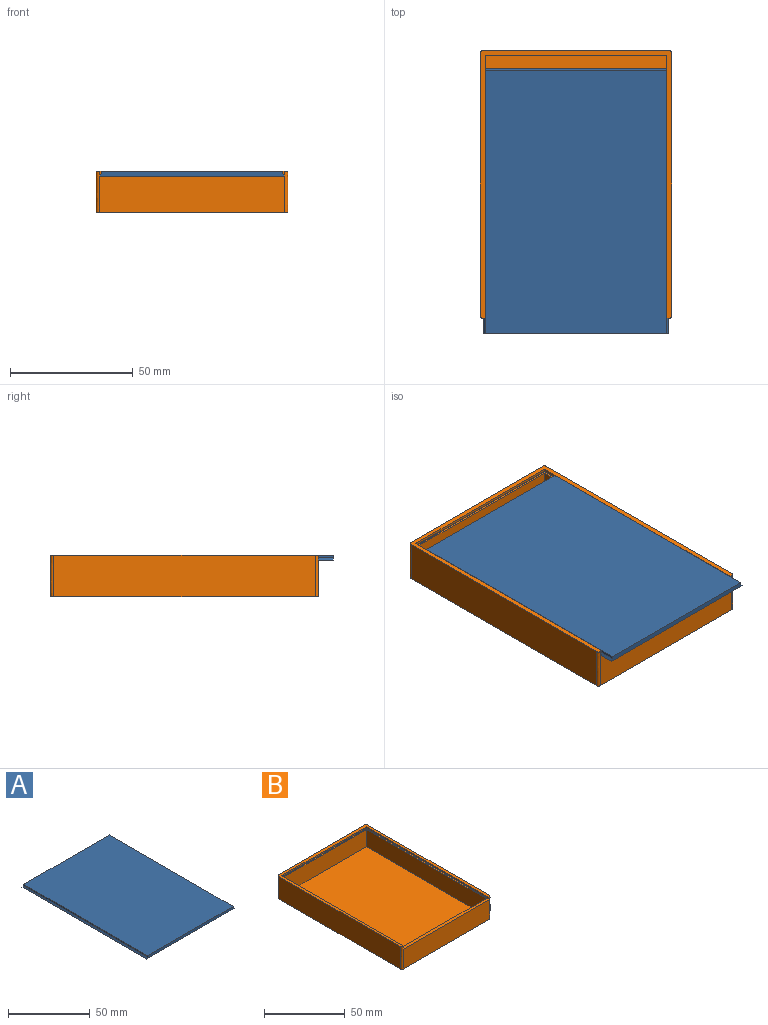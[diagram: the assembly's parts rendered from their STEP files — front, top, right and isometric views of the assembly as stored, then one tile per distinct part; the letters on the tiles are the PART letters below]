
ASSEMBLY  parts=2 mates=1
PART A: 9 faces, bbox 75.4x107.7x2 mm
  f0: plane 106.9x73.8mm, normal (0,0,1), area 7889.2mm2, adj f4,f5,f6,f8
  f1: plane 107.7x1mm, normal (-0.78,0,0.62), area 137.4mm2, adj f2,f5,f6,f7
  f2: plane 107.7x75.4mm, normal (0,0,-1), area 8120.6mm2, adj f1,f3,f6,f7
  f3: plane 107.7x1mm, normal (0.78,0,0.62), area 137.4mm2, adj f2,f4,f6,f7
  f4: plane 106.9x1mm, normal (1,0,0), area 106.9mm2, adj f0,f3,f6,f8
  f5: plane 106.9x1mm, normal (-1,0,0), area 106.9mm2, adj f0,f1,f6,f8
  f6: plane 75.4x2mm, normal (0,-1,0), area 148.4mm2, adj f0,f1,f2,f3,f4,f5
  f7: plane 75.4x1mm, normal (0,0.78,0.62), area 95.5mm2, adj f1,f2,f3,f8
  f8: plane 73.8x1mm, normal (0,1,0), area 73.8mm2, adj f0,f4,f5,f7
PART B: 243 faces, bbox 78x109x18.7 mm
  f0: plane 109x78mm, normal (0,0,-1), area 8437.6mm2, adj f1,f4,f5,f6,f20,f21,f22,f23
  f1: plane 75.6x15mm, normal (0,-1,0), area 1134mm2, adj f0,f3,f22,f23
  f2: plane 2x0.8mm, normal (0,-1,0), area 1.2mm2, adj f13,f14,f15,f23
  f3: plane 107.8x75.6mm, normal (0,0,1), area 379.7mm2, adj f1,f8,f10,f11,f12,f13,f17,f19
  f4: plane 106.6x17mm, normal (-1,0,0), area 1812.2mm2, adj f0,f15,f21,f23
  f5: plane 106.6x17mm, normal (1,0,0), area 1812.2mm2, adj f0,f15,f20,f22
  f6: plane 75.6x17mm, normal (0,1,0), area 1285.2mm2, adj f0,f15,f20,f21
  f7: plane 2x0.8mm, normal (0,-1,0), area 1.2mm2, adj f15,f16,f17,f22
  f8: plane 105x13mm, normal (1,0,0), area 1365mm2, adj f3,f9,f11,f12
  f9: plane 105x74mm, normal (0,0,1), area 7770mm2, adj f8,f10,f11,f12
  f10: plane 105x13mm, normal (-1,0,0), area 1365mm2, adj f3,f9,f11,f12
  f11: plane 74x13mm, normal (0,-1,0), area 962mm2, adj f3,f8,f9,f10
  f12: plane 74x13mm, normal (0,1,0), area 962mm2, adj f3,f8,f9,f10
  f13: plane 107.8x1mm, normal (0.78,0,-0.62), area 137.5mm2, adj f2,f3,f14,f19
  f14: plane 107x1mm, normal (1,0,0), area 107mm2, adj f2,f13,f15,f18
  f15: plane 109x78mm, normal (0,0,1), area 583mm2, adj f2,f4,f5,f6,f7,f14,f16,f18
  f16: plane 107x1mm, normal (-1,0,0), area 107mm2, adj f7,f15,f17,f18
  f17: plane 107.8x1mm, normal (-0.78,0,-0.62), area 137.5mm2, adj f3,f7,f16,f19
  f18: plane 74x1mm, normal (0,-1,0), area 74mm2, adj f14,f15,f16,f19
  f19: plane 75.6x1mm, normal (0,-0.78,-0.62), area 95.8mm2, adj f3,f13,f17,f18
  f20: bspline ~18.7x1.2mm, area 33.1mm2, adj f0,f5,f6,f15
  f21: bspline ~18.7x1.2mm, area 33.1mm2, adj f0,f4,f6,f15
  f22: bspline ~18.7x1.2mm, area 33.1mm2, adj f0,f1,f5,f7,f15
  f23: bspline ~18.7x1.2mm, area 33.1mm2, adj f0,f1,f2,f4,f15
  f24: plane 4.92x1.71mm, normal (0.33,0.94,0), area 5.2mm2, adj f0,f25,f30,f31
  f25: plane 1x0.8mm, normal (1,0,0), area 0.8mm2, adj f0,f24,f26,f31
  f26: plane 4.92x1.72mm, normal (0.33,-0.94,0), area 5.2mm2, adj f0,f25,f27,f31
  f27: plane 1x0.84mm, normal (-1,0,0), area 0.8mm2, adj f0,f26,f28,f31
  f28: plane 3.69x1.29mm, normal (-0.33,0.94,0), area 3.9mm2, adj f0,f27,f29,f31
  f29: plane 3.69x1.28mm, normal (-0.33,-0.95,0), area 3.9mm2, adj f0,f28,f30,f31
  f30: plane 1x0.83mm, normal (-1,0,0), area 0.8mm2, adj f0,f24,f29,f31
  f31: plane 4.92x4.23mm, normal (0,0,-1), area 7.6mm2, adj f24,f25,f26,f27,f28,f29,f30
  f32: plane 1x0.9mm, normal (1,0,0), area 0.9mm2, adj f0,f33,f35,f36
  f33: plane 1x0.54mm, normal (0.33,-0.95,0), area 0.6mm2, adj f0,f32,f34,f36
  f34: plane 1.28x1mm, normal (-1,0,0), area 1.3mm2, adj f0,f33,f35,f36
  f35: plane 1x0.54mm, normal (0.34,0.94,0), area 0.6mm2, adj f0,f32,f34,f36
  f36: plane 1.28x0.54mm, normal (0,0,-1), area 0.6mm2, adj f32,f33,f34,f35
  f37: plane 1.94x1.12mm, normal (0.5,0.87,0), area 2.2mm2, adj f0,f38,f62,f63
  f38: extruded ~1x0.67mm, area 0.9mm2, adj f0,f37,f39,f63
  f39: extruded ~1x0.91mm, area 1mm2, adj f0,f38,f40,f63
  f40: extruded ~1x0.64mm, area 0.7mm2, adj f0,f39,f41,f63
  f41: extruded ~1x0.48mm, area 0.6mm2, adj f0,f40,f42,f63
  f42: extruded ~1x0.55mm, area 0.6mm2, adj f0,f41,f43,f63
  f43: extruded ~1x0.62mm, area 0.6mm2, adj f0,f42,f44,f63
  f44: plane 1x0.34mm, normal (1,0,0), area 0.3mm2, adj f0,f43,f45,f63
  f45: plane 1x0.61mm, normal (0,-1,0), area 0.6mm2, adj f0,f44,f46,f63
  f46: plane 1x0.33mm, normal (-1,0,0), area 0.3mm2, adj f0,f45,f47,f63
  f47: extruded ~1x0.5mm, area 0.5mm2, adj f0,f46,f48,f63
  f48: extruded ~1x0.29mm, area 0.4mm2, adj f0,f47,f49,f63
  f49: extruded ~1x0.3mm, area 0.3mm2, adj f0,f48,f50,f63
  f50: extruded ~1x0.28mm, area 0.3mm2, adj f0,f49,f51,f63
  f51: extruded ~1x0.5mm, area 0.5mm2, adj f0,f50,f52,f63
  f52: extruded ~1x0.32mm, area 0.4mm2, adj f0,f51,f53,f63
  f53: extruded ~1x0.27mm, area 0.3mm2, adj f0,f52,f54,f63
  f54: extruded ~1x0.29mm, area 0.3mm2, adj f0,f53,f55,f63
  f55: plane 1x0.45mm, normal (1,0,0), area 0.5mm2, adj f0,f54,f56,f63
  f56: plane 1x0.59mm, normal (0,-1,0), area 0.6mm2, adj f0,f55,f57,f63
  f57: plane 1x0.24mm, normal (-1,0,0), area 0.2mm2, adj f0,f56,f58,f63
  f58: plane 1x0.14mm, normal (-1,0,0), area 0.1mm2, adj f0,f57,f59,f63
  f59: extruded ~1x0.07mm, area 0.1mm2, adj f0,f58,f60,f63
  f60: extruded ~1x0.04mm, area 0mm2, adj f0,f59,f61,f63
  f61: plane 1.78x1mm, normal (-0.46,-0.89,0), area 2mm2, adj f0,f60,f62,f63
  f62: plane 1x0.85mm, normal (-1,0,0), area 0.8mm2, adj f0,f37,f61,f63
  f63: plane 4.92x2.27mm, normal (0,0,-1), area 4.7mm2, adj f37,f38,f39,f40,f41,f42,f43,f44
  f64: plane 4.92x1mm, normal (0,-1,0), area 4.9mm2, adj f0,f65,f67,f68
  f65: plane 1x0.8mm, normal (-1,0,0), area 0.8mm2, adj f0,f64,f66,f68
  f66: plane 4.92x1mm, normal (0,1,0), area 4.9mm2, adj f0,f65,f67,f68
  f67: plane 1x0.8mm, normal (1,0,0), area 0.8mm2, adj f0,f64,f66,f68
  f68: plane 4.92x0.8mm, normal (0,0,-1), area 3.9mm2, adj f64,f65,f66,f67
  f69: plane 1x0.56mm, normal (-0.75,0.66,0), area 0.7mm2, adj f0,f70,f73,f74
  f70: extruded ~1.26x1mm, area 1.4mm2, adj f0,f69,f71,f74
  f71: plane 1x0.66mm, normal (0,-1,0), area 0.7mm2, adj f0,f70,f72,f74
  f72: extruded ~1x0.37mm, area 0.4mm2, adj f0,f71,f73,f74
  f73: extruded ~1x0.33mm, area 0.4mm2, adj f0,f69,f72,f74
  f74: plane 1.26x1.02mm, normal (0,0,-1), area 0.8mm2, adj f69,f70,f71,f72,f73
  f75: plane 1x0.78mm, normal (0,-1,0), area 0.8mm2, adj f0,f76,f87,f88
  f76: extruded ~1x0.39mm, area 0.5mm2, adj f0,f75,f77,f88
  f77: extruded ~1x0.39mm, area 0.4mm2, adj f0,f76,f78,f88
  f78: extruded ~1x0.73mm, area 1mm2, adj f0,f77,f79,f88
  f79: plane 1x0.64mm, normal (0,-1,0), area 0.6mm2, adj f0,f78,f80,f88
  f80: extruded ~1x0.55mm, area 0.6mm2, adj f0,f79,f81,f88
  f81: extruded ~1x0.4mm, area 0.5mm2, adj f0,f80,f82,f88
  f82: extruded ~1x0.41mm, area 0.5mm2, adj f0,f81,f83,f88
  f83: extruded ~1x0.47mm, area 0.5mm2, adj f0,f82,f84,f88
  f84: extruded ~1x0.58mm, area 0.6mm2, adj f0,f83,f85,f88
  f85: extruded ~1x0.4mm, area 0.5mm2, adj f0,f84,f86,f88
  f86: extruded ~1x0.42mm, area 0.5mm2, adj f0,f85,f87,f88
  f87: extruded ~1x0.45mm, area 0.5mm2, adj f0,f75,f86,f88
  f88: plane 2.83x1.3mm, normal (0,0,-1), area 2.2mm2, adj f75,f76,f77,f78,f79,f80,f81,f82
  f89: plane 1x0.58mm, normal (0.24,-0.97,0), area 0.6mm2, adj f0,f90,f100,f101
  f90: extruded ~1x0.27mm, area 0.3mm2, adj f0,f89,f91,f101
  f91: extruded ~1x0.33mm, area 0.3mm2, adj f0,f90,f92,f101
  f92: extruded ~1x0.34mm, area 0.3mm2, adj f0,f91,f93,f101
  f93: extruded ~1x0.33mm, area 0.3mm2, adj f0,f92,f94,f101
  f94: plane 1x0.01mm, normal (-1,0,0), area 0mm2, adj f0,f93,f95,f101
  f95: plane 1x0.64mm, normal (0,1,0), area 0.6mm2, adj f0,f94,f96,f101
  f96: plane 1x0.02mm, normal (1,0,0), area 0mm2, adj f0,f95,f97,f101
  f97: extruded ~1x0.29mm, area 0.3mm2, adj f0,f96,f98,f101
  f98: extruded ~1x0.31mm, area 0.3mm2, adj f0,f97,f99,f101
  f99: extruded ~1x0.3mm, area 0.3mm2, adj f0,f98,f100,f101
  f100: extruded ~1x0.24mm, area 0.3mm2, adj f0,f89,f99,f101
  f101: plane 1.29x0.93mm, normal (0,0,-1), area 0.8mm2, adj f89,f90,f91,f92,f93,f94,f95,f96
  f102: extruded ~1x0.53mm, area 0.5mm2, adj f0,f103,f115,f116
  f103: extruded ~1x0.39mm, area 0.5mm2, adj f0,f102,f104,f116
  f104: extruded ~1x0.4mm, area 0.5mm2, adj f0,f103,f105,f116
  f105: extruded ~1x0.44mm, area 0.5mm2, adj f0,f104,f106,f116
  f106: plane 1x0.76mm, normal (0,1,0), area 0.8mm2, adj f0,f105,f107,f116
  f107: extruded ~1x0.35mm, area 0.5mm2, adj f0,f106,f108,f116
  f108: extruded ~1x0.42mm, area 0.5mm2, adj f0,f107,f109,f116
  f109: extruded ~1x0.37mm, area 0.4mm2, adj f0,f108,f110,f116
  f110: extruded ~1x0.35mm, area 0.4mm2, adj f0,f109,f111,f116
  f111: plane 1x0.7mm, normal (0,1,0), area 0.7mm2, adj f0,f110,f112,f116
  f112: extruded ~1x0.49mm, area 0.5mm2, adj f0,f111,f113,f116
  f113: extruded ~1x0.4mm, area 0.5mm2, adj f0,f112,f114,f116
  f114: extruded ~1x0.41mm, area 0.5mm2, adj f0,f113,f115,f116
  f115: extruded ~1x0.53mm, area 0.5mm2, adj f0,f102,f114,f116
  f116: plane 2.79x1.26mm, normal (0,0,-1), area 2.1mm2, adj f102,f103,f104,f105,f106,f107,f108,f109
  f117: extruded ~1x0.07mm, area 0.1mm2, adj f0,f118,f127,f128
  f118: extruded ~1x0.15mm, area 0.2mm2, adj f0,f117,f119,f128
  f119: extruded ~1x0.19mm, area 0.2mm2, adj f0,f118,f120,f128
  f120: extruded ~1x0.19mm, area 0.2mm2, adj f0,f119,f121,f128
  f121: extruded ~1x0.49mm, area 0.5mm2, adj f0,f120,f122,f128
  f122: extruded ~1x0.6mm, area 0.6mm2, adj f0,f121,f123,f128
  f123: plane 1x0.67mm, normal (0,-1,0), area 0.7mm2, adj f0,f122,f124,f128
  f124: extruded ~1x0.34mm, area 0.3mm2, adj f0,f123,f125,f128
  f125: extruded ~1x0.22mm, area 0.2mm2, adj f0,f124,f126,f128
  f126: extruded ~1x0.13mm, area 0.1mm2, adj f0,f125,f127,f128
  f127: extruded ~1x0.08mm, area 0.1mm2, adj f0,f117,f126,f128
  f128: plane 1.09x0.84mm, normal (0,0,-1), area 0.6mm2, adj f117,f118,f119,f120,f121,f122,f123,f124
  f129: plane 1.99x1mm, normal (1,0,0), area 2mm2, adj f0,f130,f132,f133
  f130: plane 1x0.61mm, normal (0,-1,0), area 0.6mm2, adj f0,f129,f131,f133
  f131: plane 1.99x1mm, normal (-1,0,0), area 2mm2, adj f0,f130,f132,f133
  f132: plane 1x0.61mm, normal (0,1,0), area 0.6mm2, adj f0,f129,f131,f133
  f133: plane 1.99x0.61mm, normal (0,0,-1), area 1.2mm2, adj f129,f130,f131,f132
  f134: plane 1x0.61mm, normal (0,-1,0), area 0.6mm2, adj f0,f135,f137,f138
  f135: plane 1.99x1mm, normal (-1,0,0), area 2mm2, adj f0,f134,f136,f138
  f136: plane 1x0.61mm, normal (0,1,0), area 0.6mm2, adj f0,f135,f137,f138
  f137: plane 1.99x1mm, normal (1,0,0), area 2mm2, adj f0,f134,f136,f138
  f138: plane 1.99x0.61mm, normal (0,0,-1), area 1.2mm2, adj f134,f135,f136,f137
  f139: plane 1x0.55mm, normal (0,1,0), area 0.5mm2, adj f0,f140,f142,f143
  f140: plane 1.78x1mm, normal (1,0,0), area 1.8mm2, adj f0,f139,f141,f143
  f141: plane 1x0.55mm, normal (0,-1,0), area 0.5mm2, adj f0,f140,f142,f143
  f142: plane 1.78x1mm, normal (-1,0,0), area 1.8mm2, adj f0,f139,f141,f143
  f143: plane 1.78x0.55mm, normal (0,0,-1), area 1mm2, adj f139,f140,f141,f142
  f144: plane 1x0.66mm, normal (0,-1,0), area 0.7mm2, adj f0,f145,f149,f150
  f145: extruded ~1x0.69mm, area 0.7mm2, adj f0,f144,f146,f150
  f146: extruded ~1x0.57mm, area 0.7mm2, adj f0,f145,f147,f150
  f147: plane 1x0.56mm, normal (0.75,0.66,0), area 0.7mm2, adj f0,f146,f148,f150
  f148: extruded ~1x0.32mm, area 0.4mm2, adj f0,f147,f149,f150
  f149: extruded ~1x0.38mm, area 0.4mm2, adj f0,f144,f148,f150
  f150: plane 1.26x1.02mm, normal (0,0,-1), area 0.8mm2, adj f144,f145,f146,f147,f148,f149
  f151: extruded ~1.05x1mm, area 1.1mm2, adj f0,f152,f168,f169
  f152: extruded ~1x0.77mm, area 0.9mm2, adj f0,f151,f153,f169
  f153: extruded ~1x0.6mm, area 0.8mm2, adj f0,f152,f154,f169
  f154: extruded ~1x0.75mm, area 0.8mm2, adj f0,f153,f155,f169
  f155: plane 1x0.66mm, normal (0,1,0), area 0.7mm2, adj f0,f154,f156,f169
  f156: extruded ~1x0.41mm, area 0.4mm2, adj f0,f155,f157,f169
  f157: extruded ~1x0.35mm, area 0.5mm2, adj f0,f156,f158,f169
  f158: extruded ~1x0.56mm, area 0.6mm2, adj f0,f157,f159,f169
  f159: extruded ~1x0.8mm, area 0.8mm2, adj f0,f158,f160,f169
  f160: extruded ~1x0.8mm, area 0.8mm2, adj f0,f159,f161,f169
  f161: extruded ~1x0.56mm, area 0.6mm2, adj f0,f160,f162,f169
  f162: extruded ~1x0.34mm, area 0.5mm2, adj f0,f161,f163,f169
  f163: extruded ~1x0.41mm, area 0.4mm2, adj f0,f162,f164,f169
  f164: plane 1x0.67mm, normal (0,1,0), area 0.7mm2, adj f0,f163,f165,f169
  f165: extruded ~1x0.75mm, area 0.8mm2, adj f0,f164,f166,f169
  f166: extruded ~1x0.6mm, area 0.8mm2, adj f0,f165,f167,f169
  f167: extruded ~1x0.77mm, area 0.9mm2, adj f0,f166,f168,f169
  f168: extruded ~1.05x1mm, area 1.1mm2, adj f0,f151,f167,f169
  f169: plane 5.02x1.89mm, normal (0,0,-1), area 4.4mm2, adj f151,f152,f153,f154,f155,f156,f157,f158
  f170: plane 2.36x1mm, normal (0,1,0), area 2.4mm2, adj f0,f171,f181,f182
  f171: plane 1x0.81mm, normal (1,0,0), area 0.8mm2, adj f0,f170,f172,f182
  f172: plane 2.44x1mm, normal (0,-1,0), area 2.4mm2, adj f0,f171,f173,f182
  f173: extruded ~1.06x1mm, area 1.1mm2, adj f0,f172,f174,f182
  f174: extruded ~1x0.78mm, area 0.9mm2, adj f0,f173,f175,f182
  f175: extruded ~1x0.56mm, area 0.7mm2, adj f0,f174,f176,f182
  f176: extruded ~1x0.74mm, area 0.8mm2, adj f0,f175,f177,f182
  f177: plane 1x0.66mm, normal (0,1,0), area 0.7mm2, adj f0,f176,f178,f182
  f178: extruded ~1x0.4mm, area 0.4mm2, adj f0,f177,f179,f182
  f179: extruded ~1x0.34mm, area 0.5mm2, adj f0,f178,f180,f182
  f180: extruded ~1x0.59mm, area 0.6mm2, adj f0,f179,f181,f182
  f181: extruded ~1x0.87mm, area 0.9mm2, adj f0,f170,f180,f182
  f182: plane 4.96x1.78mm, normal (0,0,-1), area 4.1mm2, adj f170,f171,f172,f173,f174,f175,f176,f177
  f183: plane 1x0.81mm, normal (1,0,0), area 0.8mm2, adj f0,f184,f194,f195
  f184: plane 2.36x1mm, normal (0,-1,0), area 2.4mm2, adj f0,f183,f185,f195
  f185: extruded ~1x0.88mm, area 0.9mm2, adj f0,f184,f186,f195
  f186: extruded ~1x0.58mm, area 0.6mm2, adj f0,f185,f187,f195
  f187: extruded ~1x0.34mm, area 0.5mm2, adj f0,f186,f188,f195
  f188: extruded ~1x0.4mm, area 0.4mm2, adj f0,f187,f189,f195
  f189: plane 1x0.66mm, normal (0,-1,0), area 0.7mm2, adj f0,f188,f190,f195
  f190: extruded ~1x0.74mm, area 0.8mm2, adj f0,f189,f191,f195
  f191: extruded ~1x0.56mm, area 0.7mm2, adj f0,f190,f192,f195
  f192: extruded ~1x0.78mm, area 0.9mm2, adj f0,f191,f193,f195
  f193: extruded ~1.06x1mm, area 1.1mm2, adj f0,f192,f194,f195
  f194: plane 2.44x1mm, normal (0,1,0), area 2.4mm2, adj f0,f183,f193,f195
  f195: plane 4.96x1.78mm, normal (0,0,-1), area 4.1mm2, adj f183,f184,f185,f186,f187,f188,f189,f190
  f196: plane 1x0.82mm, normal (1,0,0), area 0.8mm2, adj f0,f197,f201,f202
  f197: plane 4.92x1mm, normal (0,-1,0), area 4.9mm2, adj f0,f196,f198,f202
  f198: plane 3.08x1mm, normal (-1,0,0), area 3.1mm2, adj f0,f197,f199,f202
  f199: plane 1x0.61mm, normal (0,1,0), area 0.6mm2, adj f0,f198,f200,f202
  f200: plane 2.27x1mm, normal (1,0,0), area 2.3mm2, adj f0,f199,f201,f202
  f201: plane 4.32x1mm, normal (0,1,0), area 4.3mm2, adj f0,f196,f200,f202
  f202: plane 4.92x3.08mm, normal (0,0,-1), area 5.4mm2, adj f196,f197,f198,f199,f200,f201
  f203: plane 3.75x1mm, normal (1,0,0), area 3.7mm2, adj f0,f204,f210,f211
  f204: plane 1x0.55mm, normal (0,-1,0), area 0.5mm2, adj f0,f203,f205,f211
  f205: plane 1.47x1mm, normal (-1,0,0), area 1.5mm2, adj f0,f204,f206,f211
  f206: plane 4.38x1mm, normal (0,-1,0), area 4.4mm2, adj f0,f205,f207,f211
  f207: plane 1x0.81mm, normal (-1,0,0), area 0.8mm2, adj f0,f206,f208,f211
  f208: plane 4.38x1mm, normal (0,1,0), area 4.4mm2, adj f0,f207,f209,f211
  f209: plane 1.47x1mm, normal (-1,0,0), area 1.5mm2, adj f0,f208,f210,f211
  f210: plane 1x0.55mm, normal (0,1,0), area 0.5mm2, adj f0,f203,f209,f211
  f211: plane 4.92x3.75mm, normal (0,0,-1), area 5.6mm2, adj f203,f204,f205,f206,f207,f208,f209,f210
  f212: plane 2.36x1mm, normal (0,1,0), area 2.4mm2, adj f0,f213,f223,f224
  f213: plane 1x0.81mm, normal (1,0,0), area 0.8mm2, adj f0,f212,f214,f224
  f214: plane 2.44x1mm, normal (0,-1,0), area 2.4mm2, adj f0,f213,f215,f224
  f215: extruded ~1.06x1mm, area 1.1mm2, adj f0,f214,f216,f224
  f216: extruded ~1x0.78mm, area 0.9mm2, adj f0,f215,f217,f224
  f217: extruded ~1x0.56mm, area 0.7mm2, adj f0,f216,f218,f224
  f218: extruded ~1x0.74mm, area 0.8mm2, adj f0,f217,f219,f224
  f219: plane 1x0.66mm, normal (0,1,0), area 0.7mm2, adj f0,f218,f220,f224
  f220: extruded ~1x0.4mm, area 0.4mm2, adj f0,f219,f221,f224
  f221: extruded ~1x0.34mm, area 0.5mm2, adj f0,f220,f222,f224
  f222: extruded ~1x0.59mm, area 0.6mm2, adj f0,f221,f223,f224
  f223: extruded ~1x0.87mm, area 0.9mm2, adj f0,f212,f222,f224
  f224: plane 4.96x1.78mm, normal (0,0,-1), area 4.1mm2, adj f212,f213,f214,f215,f216,f217,f218,f219
  f225: plane 1x0.81mm, normal (1,0,0), area 0.8mm2, adj f0,f226,f236,f237
  f226: plane 2.36x1mm, normal (0,-1,0), area 2.4mm2, adj f0,f225,f227,f237
  f227: extruded ~1x0.88mm, area 0.9mm2, adj f0,f226,f228,f237
  f228: extruded ~1x0.58mm, area 0.6mm2, adj f0,f227,f229,f237
  f229: extruded ~1x0.34mm, area 0.5mm2, adj f0,f228,f230,f237
  f230: extruded ~1x0.4mm, area 0.4mm2, adj f0,f229,f231,f237
  f231: plane 1x0.66mm, normal (0,-1,0), area 0.7mm2, adj f0,f230,f232,f237
  f232: extruded ~1x0.74mm, area 0.8mm2, adj f0,f231,f233,f237
  f233: extruded ~1x0.56mm, area 0.7mm2, adj f0,f232,f234,f237
  f234: extruded ~1x0.78mm, area 0.9mm2, adj f0,f233,f235,f237
  f235: extruded ~1.06x1mm, area 1.1mm2, adj f0,f234,f236,f237
  f236: plane 2.44x1mm, normal (0,1,0), area 2.4mm2, adj f0,f225,f235,f237
  f237: plane 4.96x1.78mm, normal (0,0,-1), area 4.1mm2, adj f225,f226,f227,f228,f229,f230,f231,f232
  f238: plane 4.92x1mm, normal (0,-1,0), area 4.9mm2, adj f0,f239,f241,f242
  f239: plane 1x0.81mm, normal (-1,0,0), area 0.8mm2, adj f0,f238,f240,f242
  f240: plane 4.92x1mm, normal (0,1,0), area 4.9mm2, adj f0,f239,f241,f242
  f241: plane 1x0.81mm, normal (1,0,0), area 0.8mm2, adj f0,f238,f240,f242
  f242: plane 4.92x0.81mm, normal (0,0,-1), area 4mm2, adj f238,f239,f240,f241
PLACE A t=(-22.2,-88.97,3.46)mm
PLACE B t=(-23.5,-82.87,3.46)mm fixed
MATE slider A.f8 <-> B.f18  axis (0,1,0) through (15.5,17.93,4.96)mm
